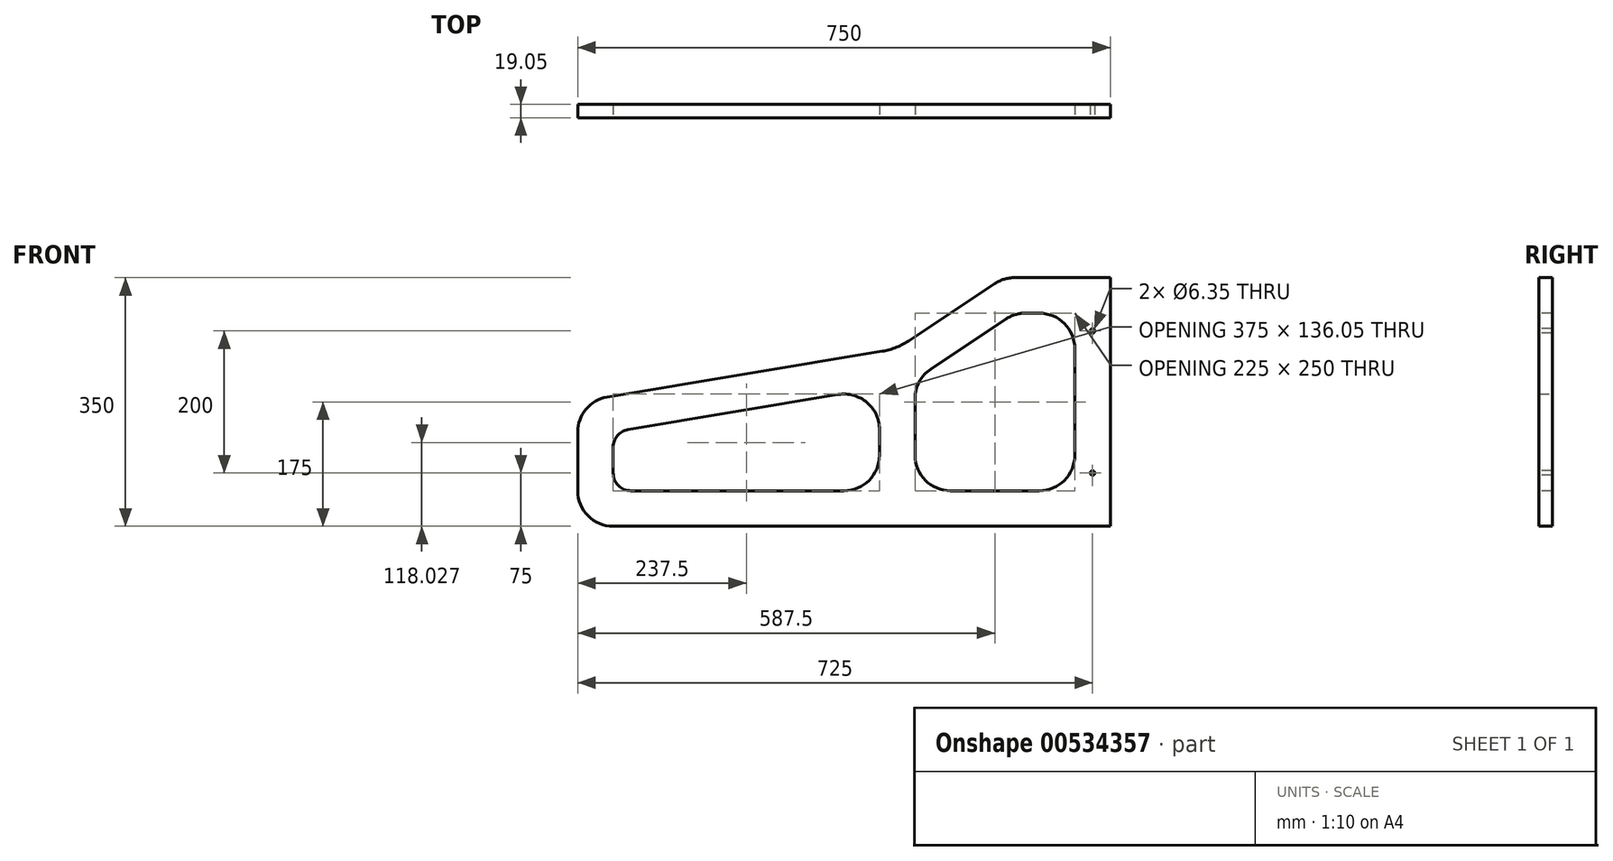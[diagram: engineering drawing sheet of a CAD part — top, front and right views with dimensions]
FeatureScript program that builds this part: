
annotation { "Feature Type Name" : "Feature", "Feature Type Description" : "" }
export const myFeature = defineFeature(function(context is Context, id is Id, definition is map)
    precondition{}
    {
        {
            var Q0;
            Q0=qCreatedBy(makeId("Front.planeOp"),FACE);
            var sketch = newSketch(context, id + "F0", { "sketchPlane" : qUnion([Q0])});
            skLineSegment(sketch, "E0", {"start": v(0, 0) * mm, "end": v(-750, 0) * mm});
            skLineSegment(sketch, "E1", {"start": v(-750, 0) * mm, "end": v(-750, 175) * mm});
            skLineSegment(sketch, "E2", {"start": v(-750, 175) * mm, "end": v(-300, 250) * mm});
            skLineSegment(sketch, "E3", {"start": v(-300, 250) * mm, "end": v(-150, 350) * mm});
            skLineSegment(sketch, "E4", {"start": v(-150, 350) * mm, "end": v(0, 350) * mm});
            skLineSegment(sketch, "E5", {"start": v(0, 350) * mm, "end": v(0, 0) * mm});
            skSolve(sketch);
        }
        {
            var Q0;
            Q0=makeQuery(id+"F0.imprint","IMPRINT",FACE,{"disambiguationData":[TD([[makeQuery(id+"F0.imprint","IMPRINT",EDGE,{"derivedFrom":sQuery(id+"F0.wireOp",EDGE,"E0")}),-1.0]])]});
            extrude(context, id + "F1", {"entities" : qUnion([Q0]), "depth" : 19.05 * mm, "offsetDistance" : 25 * mm});
        }
        {
            var Q0;
            Q0=makeQuery(id+"F1.opExtrude","CAP_FACE",FACE,{"disambiguationData":[OSD([sQuery(id+"F0.wireOp",EDGE,"E0"),sQuery(id+"F0.wireOp",EDGE,"E1"),sQuery(id+"F0.wireOp",EDGE,"E2"),sQuery(id+"F0.wireOp",EDGE,"E3"),sQuery(id+"F0.wireOp",EDGE,"E4"),sQuery(id+"F0.wireOp",EDGE,"E5")])],"isStart":false});
            var sketch = newSketch(context, id + "F2", { "sketchPlane" : qUnion([Q0])});
            skLineSegment(sketch, "E6", {"start": v(-700, 132.64) * mm, "end": v(-700, 50) * mm});
            skLineSegment(sketch, "E7", {"start": v(-700, 50) * mm, "end": v(-325, 50) * mm});
            skLineSegment(sketch, "E8", {"start": v(-325, 50) * mm, "end": v(-325, 195.14) * mm});
            skLineSegment(sketch, "E9", {"start": v(-325, 195.14) * mm, "end": v(-700, 132.64) * mm});
            skLineSegment(sketch, "E10", {"start": v(-275, 206.57) * mm, "end": v(-275, 50) * mm});
            skLineSegment(sketch, "E11", {"start": v(-275, 50) * mm, "end": v(-50, 50) * mm});
            skLineSegment(sketch, "E12", {"start": v(-50, 50) * mm, "end": v(-50, 300) * mm});
            skLineSegment(sketch, "E13", {"start": v(-50, 300) * mm, "end": v(-134.86, 300) * mm});
            skLineSegment(sketch, "E14", {"start": v(-134.86, 300) * mm, "end": v(-275, 206.57) * mm});
            skSolve(sketch);
        }
        {
            var Q0;
            Q0=makeQuery(id+"F2.imprint","IMPRINT",FACE,{"disambiguationData":[TD([[makeQuery(id+"F2.imprint","IMPRINT",EDGE,{"derivedFrom":sQuery(id+"F2.wireOp",EDGE,"E6")}),1.0]])]});
            var Q1;
            Q1=makeQuery(id+"F2.imprint","IMPRINT",FACE,{"disambiguationData":[TD([[makeQuery(id+"F2.imprint","IMPRINT",EDGE,{"derivedFrom":sQuery(id+"F2.wireOp",EDGE,"E10")}),1.0]])]});
            extrude(context, id + "F3", {"entities" : qUnion([Q0, Q1]), "operationType" : NewBodyOperationType.REMOVE, "oppositeDirection" : true, "depth" : 25 * mm, "offsetDistance" : 25 * mm});
        }
        {
            var Q0;
            Q0=makeQuery(id+"F3.boolean.opBoolean","COPY",EDGE,{"derivedFrom":makeQuery(id+"F3.opExtrude","SWEPT_EDGE",EDGE,{"disambiguationData":[OSD([sQuery(id+"F2.wireOp",EDGE,"E8"),sQuery(id+"F2.wireOp",EDGE,"E9")])]})});
            var Q1;
            Q1=makeQuery(id+"F3.boolean.opBoolean","COPY",EDGE,{"derivedFrom":makeQuery(id+"F3.opExtrude","SWEPT_EDGE",EDGE,{"disambiguationData":[OSD([sQuery(id+"F2.wireOp",EDGE,"E7"),sQuery(id+"F2.wireOp",EDGE,"E8")])]})});
            var Q2;
            Q2=makeQuery(id+"F3.boolean.opBoolean","COPY",EDGE,{"derivedFrom":makeQuery(id+"F3.opExtrude","SWEPT_EDGE",EDGE,{"disambiguationData":[OSD([sQuery(id+"F2.wireOp",EDGE,"E10"),sQuery(id+"F2.wireOp",EDGE,"E14")])]})});
            var Q3;
            Q3=makeQuery(id+"F3.boolean.opBoolean","COPY",EDGE,{"derivedFrom":makeQuery(id+"F3.opExtrude","SWEPT_EDGE",EDGE,{"disambiguationData":[OSD([sQuery(id+"F2.wireOp",EDGE,"E13"),sQuery(id+"F2.wireOp",EDGE,"E14")])]})});
            var Q4;
            Q4=makeQuery(id+"F3.boolean.opBoolean","COPY",EDGE,{"derivedFrom":makeQuery(id+"F3.opExtrude","SWEPT_EDGE",EDGE,{"disambiguationData":[OSD([sQuery(id+"F2.wireOp",EDGE,"E12"),sQuery(id+"F2.wireOp",EDGE,"E13")])]})});
            var Q5;
            Q5=makeQuery(id+"F3.boolean.opBoolean","COPY",EDGE,{"derivedFrom":makeQuery(id+"F3.opExtrude","SWEPT_EDGE",EDGE,{"disambiguationData":[OSD([sQuery(id+"F2.wireOp",EDGE,"E11"),sQuery(id+"F2.wireOp",EDGE,"E12")])]})});
            var Q6;
            Q6=makeQuery(id+"F3.boolean.opBoolean","COPY",EDGE,{"derivedFrom":makeQuery(id+"F3.opExtrude","SWEPT_EDGE",EDGE,{"disambiguationData":[OSD([sQuery(id+"F2.wireOp",EDGE,"E10"),sQuery(id+"F2.wireOp",EDGE,"E11")])]})});
            fillet(context, id + "F4", {"entities" : qUnion([Q0, Q1, Q2, Q3, Q4, Q5, Q6]), "radius" : 50 * mm, "tangentPropagation" : true, "allowEdgeOverflow" : false});
        }
        {
            var Q0;
            Q0=makeQuery(id+"F3.boolean.opBoolean","COPY",EDGE,{"derivedFrom":makeQuery(id+"F3.opExtrude","SWEPT_EDGE",EDGE,{"disambiguationData":[OSD([sQuery(id+"F2.wireOp",EDGE,"E6"),sQuery(id+"F2.wireOp",EDGE,"E9")])]})});
            var Q1;
            Q1=makeQuery(id+"F3.boolean.opBoolean","COPY",EDGE,{"derivedFrom":makeQuery(id+"F3.opExtrude","SWEPT_EDGE",EDGE,{"disambiguationData":[OSD([sQuery(id+"F2.wireOp",EDGE,"E6"),sQuery(id+"F2.wireOp",EDGE,"E7")])]})});
            fillet(context, id + "F5", {"entities" : qUnion([Q0, Q1]), "radius" : 25 * mm, "tangentPropagation" : true, "allowEdgeOverflow" : false});
        }
        {
            var Q0;
            Q0=makeQuery(id+"F1.opExtrude","SWEPT_EDGE",EDGE,{"disambiguationData":[OSD([sQuery(id+"F0.wireOp",EDGE,"E1"),sQuery(id+"F0.wireOp",EDGE,"E2")])]});
            var Q1;
            Q1=makeQuery(id+"F1.opExtrude","SWEPT_EDGE",EDGE,{"disambiguationData":[OSD([sQuery(id+"F0.wireOp",EDGE,"E0"),sQuery(id+"F0.wireOp",EDGE,"E1")])]});
            var Q2;
            Q2=makeQuery(id+"F1.opExtrude","SWEPT_EDGE",EDGE,{"disambiguationData":[OSD([sQuery(id+"F0.wireOp",EDGE,"E3"),sQuery(id+"F0.wireOp",EDGE,"E4")])]});
            fillet(context, id + "F6", {"entities" : qUnion([Q0, Q1, Q2]), "radius" : 50 * mm, "tangentPropagation" : true, "allowEdgeOverflow" : false});
        }
        {
            var Q0;
            Q0=makeQuery(id+"F1.opExtrude","CAP_FACE",FACE,{"disambiguationData":[OSD([sQuery(id+"F0.wireOp",EDGE,"E0"),sQuery(id+"F0.wireOp",EDGE,"E1"),sQuery(id+"F0.wireOp",EDGE,"E2"),sQuery(id+"F0.wireOp",EDGE,"E3"),sQuery(id+"F0.wireOp",EDGE,"E4"),sQuery(id+"F0.wireOp",EDGE,"E5")])],"isStart":false});
            var sketch = newSketch(context, id + "F7", { "sketchPlane" : qUnion([Q0])});
            skCircle(sketch, "E15", {"center": v(-25, 275) * mm, "radius": 3.17 * mm});
            skCircle(sketch, "E16", {"center": v(-25, 75) * mm, "radius": 3.17 * mm});
            skSolve(sketch);
        }
        {
            var Q0;
            Q0=makeQuery(id+"F7.imprint","IMPRINT",FACE,{"disambiguationData":[TD([[makeQuery(id+"F7.imprint","IMPRINT",EDGE,{"derivedFrom":sQuery(id+"F7.wireOp",EDGE,"E15")}),1.0]])]});
            var Q1;
            Q1=makeQuery(id+"F7.imprint","IMPRINT",FACE,{"disambiguationData":[TD([[makeQuery(id+"F7.imprint","IMPRINT",EDGE,{"derivedFrom":sQuery(id+"F7.wireOp",EDGE,"E16")}),1.0]])]});
            extrude(context, id + "F8", {"entities" : qUnion([Q0, Q1]), "operationType" : NewBodyOperationType.REMOVE, "oppositeDirection" : true, "depth" : 25 * mm, "offsetDistance" : 25 * mm});
        }
        {
            var Q0;
            Q0=makeQuery(id+"F1.opExtrude","SWEPT_EDGE",EDGE,{"disambiguationData":[OSD([sQuery(id+"F0.wireOp",EDGE,"E2"),sQuery(id+"F0.wireOp",EDGE,"E3")])]});
            fillet(context, id + "F9", {"entities" : qUnion([Q0]), "radius" : 100 * mm, "tangentPropagation" : true, "allowEdgeOverflow" : false});
        }
    });
